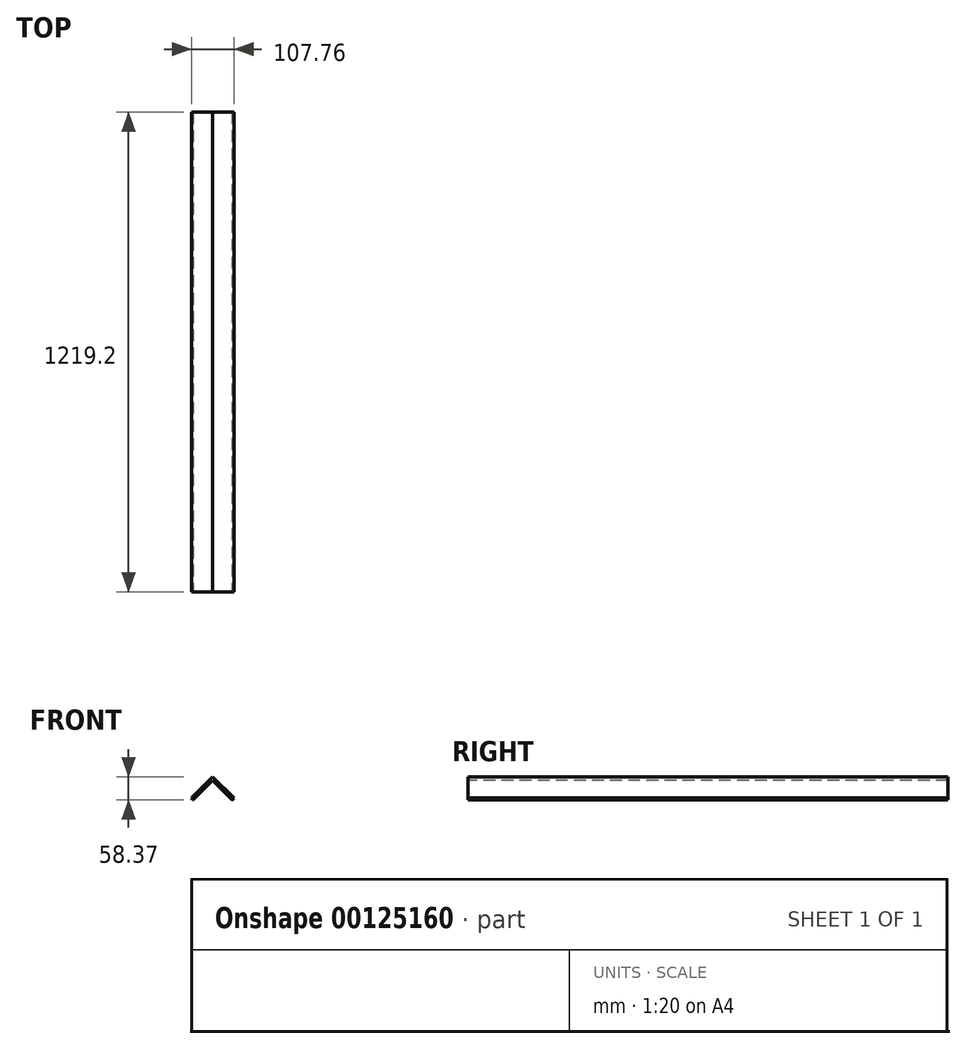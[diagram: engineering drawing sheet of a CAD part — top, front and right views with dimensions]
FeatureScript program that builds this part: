
annotation { "Feature Type Name" : "Feature", "Feature Type Description" : "" }
export const myFeature = defineFeature(function(context is Context, id is Id, definition is map)
    precondition{}
    {
        {
            var Q0;
            Q0=qCreatedBy(makeId("Front.planeOp"),FACE);
            var sketch = newSketch(context, id + "F0", { "sketchPlane" : qUnion([Q0])});
            skLineSegment(sketch, "E0", {"start": v(0, 0) * mm, "end": v(53.88, 53.88) * mm});
            skLineSegment(sketch, "E1", {"start": v(53.88, 53.88) * mm, "end": v(107.76, 0) * mm});
            skLineSegment(sketch, "E2.0", {"start": v(53.88, 44.9) * mm, "end": v(103.27, -4.5) * mm});
            skLineSegment(sketch, "E2.1", {"start": v(4.5, -4.5) * mm, "end": v(53.88, 44.9) * mm});
            skLineSegment(sketch, "E3", {"start": v(4.5, -4.5) * mm, "end": v(2.9, -4.5) * mm});
            skLineSegment(sketch, "E4", {"start": v(103.27, -4.5) * mm, "end": v(104.86, -4.5) * mm});
            skLineSegment(sketch, "E5", {"start": v(104.86, -4.5) * mm, "end": v(107.76, 0) * mm});
            skLineSegment(sketch, "E6", {"start": v(2.9, -4.5) * mm, "end": v(0, 0) * mm});
            skSolve(sketch);
        }
        {
            var Q0;
            Q0=qSketchRegion(id+"F0",true);
            extrude(context, id + "F1", {"entities" : qUnion([Q0]), "oppositeDirection" : true, "depth" : 1219.2 * mm});
        }
    });
